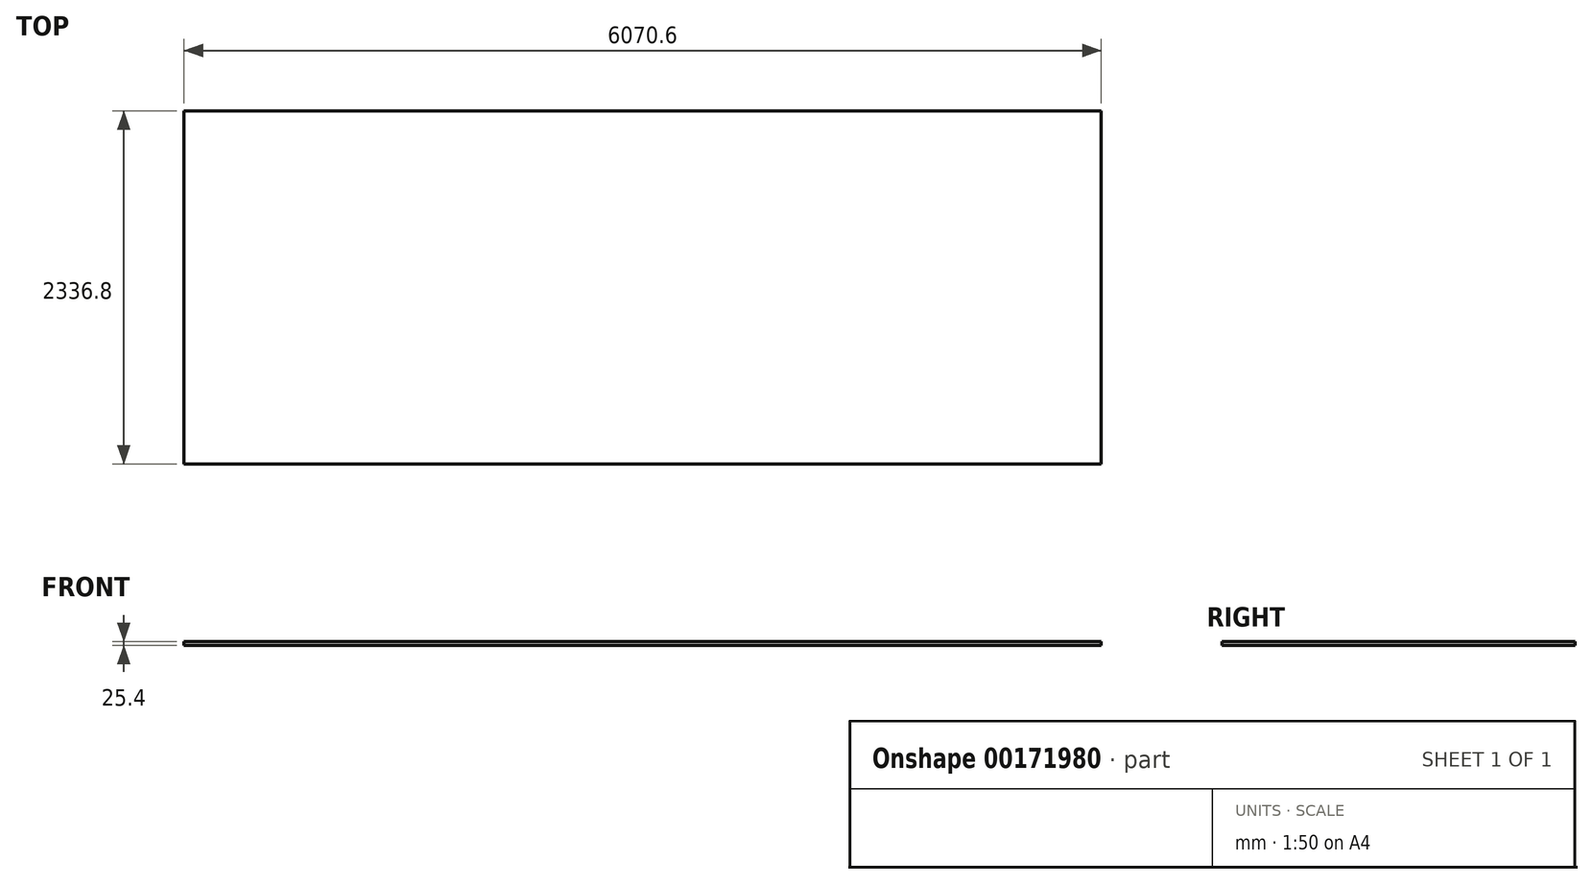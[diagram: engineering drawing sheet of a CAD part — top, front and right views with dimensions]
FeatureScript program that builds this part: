
annotation { "Feature Type Name" : "Feature", "Feature Type Description" : "" }
export const myFeature = defineFeature(function(context is Context, id is Id, definition is map)
    precondition{}
    {
        {
            var Q0;
            Q0=qCreatedBy(makeId("Top.planeOp"),FACE);
            var sketch = newSketch(context, id + "F0", { "sketchPlane" : qUnion([Q0])});
            skLineSegment(sketch, "E0.bottom", {"start": v(3035.3, 1168.4) * mm, "end": v(-3035.3, 1168.4) * mm});
            skLineSegment(sketch, "E0.top", {"start": v(3035.3, -1168.4) * mm, "end": v(-3035.3, -1168.4) * mm});
            skLineSegment(sketch, "E0.left", {"start": v(3035.3, 1168.4) * mm, "end": v(3035.3, -1168.4) * mm});
            skLineSegment(sketch, "E0.right", {"start": v(-3035.3, 1168.4) * mm, "end": v(-3035.3, -1168.4) * mm});
            skPoint(sketch, "E0.middle", {"position": v(0, 0) * mm});
            skSolve(sketch);
        }
        {
            var Q0;
            Q0 = qSketchRegion(id + "F0", true);
            extrude(context, id + "F1", {"entities" : qUnion([Q0]), "depth" : 25.4 * mm});
        }
    });
